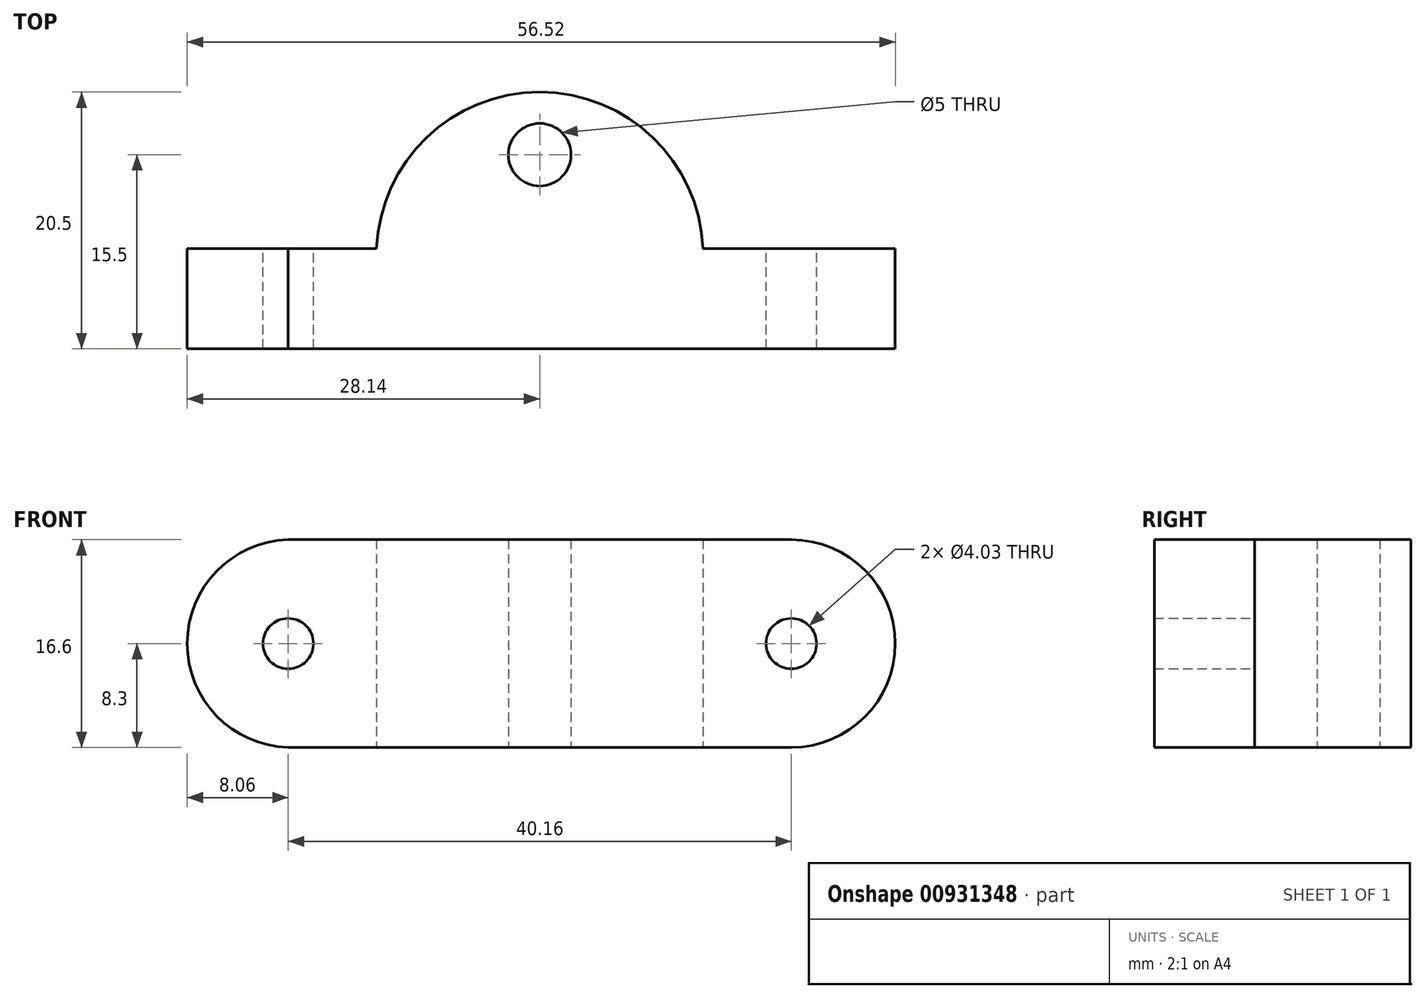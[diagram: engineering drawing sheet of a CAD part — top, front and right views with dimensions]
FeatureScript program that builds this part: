
annotation { "Feature Type Name" : "Feature", "Feature Type Description" : "" }
export const myFeature = defineFeature(function(context is Context, id is Id, definition is map)
    precondition{}
    {
        {
            var Q0;
            Q0=qCreatedBy(makeId("Front.planeOp"),FACE);
            var sketch = newSketch(context, id + "F0", { "sketchPlane" : qUnion([Q0])});
            skLineSegment(sketch, "E0", {"start": v(-20.08, 8.3) * mm, "end": v(20.08, 8.3) * mm});
            skLineSegment(sketch, "E1", {"start": v(-20.08, -8.3) * mm, "end": v(20.08, -8.3) * mm});
            skPoint(sketch, "E2", {"position": v(-20.08, 0) * mm});
            skPoint(sketch, "E3", {"position": v(20.08, 0) * mm});
            skArc(sketch, "E4", {"start": v(-20.08, 8.3) * mm, "mid": v(-28.14, 0) * mm, "end": v(-20.08, -8.3) * mm});
            skArc(sketch, "E5", {"start": v(20.08, -8.3) * mm, "mid": v(28.38, 0) * mm, "end": v(20.08, 8.3) * mm});
            skCircle(sketch, "E6", {"center": v(20.08, 0) * mm, "radius": 2.02 * mm});
            skLineSegment(sketch, "E7", {"start": v(-28.14, 0) * mm, "end": v(28.38, 0) * mm});
            skCircle(sketch, "E8.MirrorC", {"center": v(-20.08, 0) * mm, "radius": 2.02 * mm});
            skSolve(sketch);
        }
        {
            var Q0;
            Q0 = qSketchRegion(id + "F0", true);
            extrude(context, id + "F1", {"entities" : qUnion([Q0]), "depth" : 8 * mm, "offsetDistance" : 25 * mm});
        }
        {
            var Q0;
            Q0=qCreatedBy(makeId("Top.planeOp"),FACE);
            var sketch = newSketch(context, id + "F2", { "sketchPlane" : qUnion([Q0])});
            skLineSegment(sketch, "E9", {"start": v(-13.03, 0) * mm, "end": v(13.03, 0) * mm, "construction": true});
            skArc(sketch, "E10", {"start": v(13.03, 0) * mm, "mid": v(0, 12.5) * mm, "end": v(-13.03, 0) * mm});
            skCircle(sketch, "E11", {"center": v(0, 7.5) * mm, "radius": 2.5 * mm});
            skLineSegment(sketch, "E12", {"start": v(-13.03, 0) * mm, "end": v(13.03, 0) * mm});
            skLineSegment(sketch, "E13", {"start": v(0, 5) * mm, "end": v(0, -8) * mm, "construction": true});
            skSolve(sketch);
        }
        {
            var Q0;
            Q0=makeQuery(id+"F2.imprint","IMPRINT",FACE,{"disambiguationData":[TD([[makeQuery(id+"F2.imprint","IMPRINT",EDGE,{"derivedFrom":sQuery(id+"F2.wireOp",EDGE,"E10")}),1.0]])]});
            var Q1;
            Q1=makeQuery(id+"F1.opExtrude","SWEPT_FACE",FACE,{"disambiguationData":[OSD([sQuery(id+"F0.wireOp",EDGE,"E0")])]});
            var Q2;
            Q2=makeQuery(id+"F1.opExtrude","SWEPT_FACE",FACE,{"disambiguationData":[OSD([sQuery(id+"F0.wireOp",EDGE,"E1")])]});
            extrude(context, id + "F3", {"entities" : qUnion([Q0]), "operationType" : NewBodyOperationType.ADD, "endBound" : BoundingType.UP_TO_SURFACE, "depth" : 25 * mm, "endBoundEntityFace" : qUnion([Q1]), "offsetDistance" : 25 * mm, "hasSecondDirection" : true, "secondDirectionBound" : SecondDirectionBoundingType.UP_TO_SURFACE, "secondDirectionOppositeDirection" : true, "secondDirectionDepth" : 25 * mm, "secondDirectionBoundEntityFace" : qUnion([Q2])});
        }
    });
